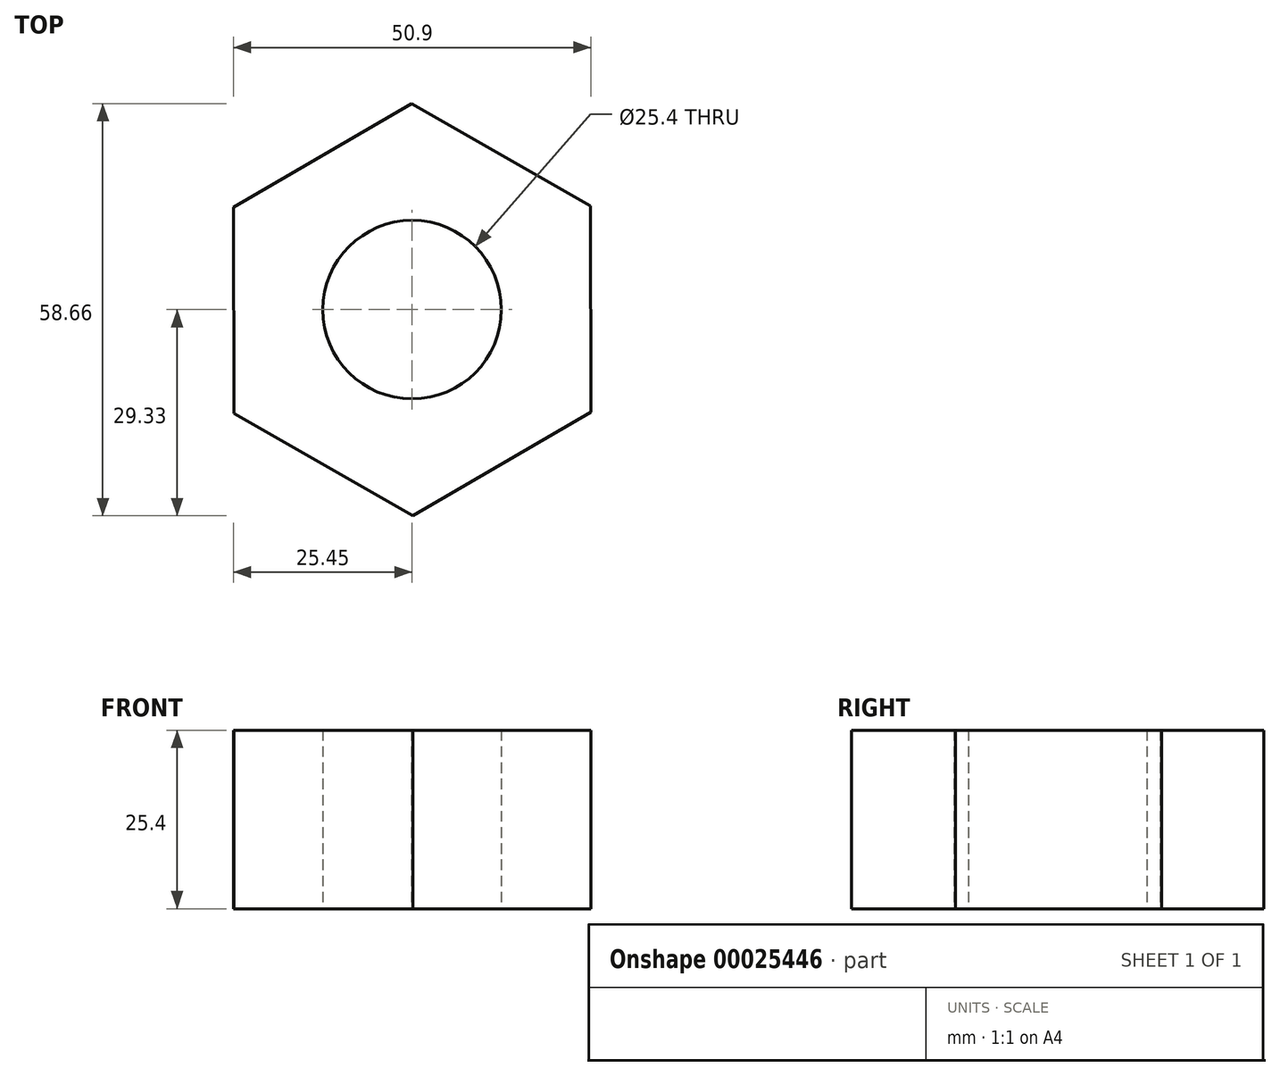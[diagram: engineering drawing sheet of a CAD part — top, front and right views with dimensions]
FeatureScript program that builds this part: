
annotation { "Feature Type Name" : "Feature", "Feature Type Description" : "" }
export const myFeature = defineFeature(function(context is Context, id is Id, definition is map)
    precondition{}
    {
        {
            var Q0;
            Q0=qCreatedBy(makeId("Top.planeOp"),FACE);
            var sketch = newSketch(context, id + "F0", { "sketchPlane" : qUnion([Q0])});
            skCircle(sketch, "E0", {"center": v(0, 0) * mm, "radius": 12.7 * mm});
            skCircle(sketch, "E1", {"center": v(0, 0) * mm, "radius": 25.4 * mm});
            skCircle(sketch, "E2.cCircle", {"center": v(0, 0) * mm, "radius": 25.4 * mm, "construction": true});
            skLineSegment(sketch, "E2.0", {"start": v(-25.45, 14.58) * mm, "end": v(-0.1, 29.33) * mm});
            skLineSegment(sketch, "E2.1", {"start": v(-0.1, 29.33) * mm, "end": v(25.35, 14.75) * mm});
            skLineSegment(sketch, "E2.2", {"start": v(25.35, 14.75) * mm, "end": v(25.45, -14.58) * mm});
            skLineSegment(sketch, "E2.3", {"start": v(25.45, -14.58) * mm, "end": v(0.1, -29.33) * mm});
            skLineSegment(sketch, "E2.4", {"start": v(0.1, -29.33) * mm, "end": v(-25.35, -14.75) * mm});
            skLineSegment(sketch, "E2.5", {"start": v(-25.35, -14.75) * mm, "end": v(-25.45, 14.58) * mm});
            skPoint(sketch, "E2.0.midPoint", {"position": v(-12.78, 21.95) * mm});
            skSolve(sketch);
        }
        {
            var Q0;
            Q0=makeQuery(id+"F0.imprint","IMPRINT",FACE,{"disambiguationData":[TD([[makeQuery(id+"F0.imprint","IMPRINT",EDGE,{"derivedFrom":sQuery(id+"F0.wireOp",EDGE,"E0")}),-1.0]])]});
            var Q1;
            {var subQ0=sQuery(id+"F0.wireOp",EDGE,"E2.5");var subQ1=sQuery(id+"F0.wireOp",EDGE,"E1");var subQ2=makeQuery(id+"F0.imprint","INTERSECT",VERTEX,{"derivedFrom":[subQ1,subQ0]});Q1=makeQuery(id+"F0.imprint","IMPRINT",FACE,{"disambiguationData":[TD([[makeQuery(id+"F0.imprint","IMPRINT",EDGE,{"disambiguationData":[TD([[subQ2,-1.0]])],"derivedFrom":subQ1}),-1.0]])]});}
            var Q2;
            {var subQ0=sQuery(id+"F0.wireOp",EDGE,"E2.4");var subQ1=sQuery(id+"F0.wireOp",EDGE,"E1");var subQ2=makeQuery(id+"F0.imprint","INTERSECT",VERTEX,{"derivedFrom":[subQ1,subQ0]});Q2=makeQuery(id+"F0.imprint","IMPRINT",FACE,{"disambiguationData":[TD([[makeQuery(id+"F0.imprint","IMPRINT",EDGE,{"disambiguationData":[TD([[subQ2,-1.0]])],"derivedFrom":subQ1}),-1.0]])]});}
            var Q3;
            {var subQ1=sQuery(id+"F0.wireOp",EDGE,"E1");var subQ3=sQuery(id+"F0.wireOp",EDGE,"E2.2");var subQ5=makeQuery(id+"F0.imprint","INTERSECT",VERTEX,{"derivedFrom":[subQ1,subQ3]});Q3=makeQuery(id+"F0.imprint","IMPRINT",FACE,{"disambiguationData":[TD([[makeQuery(id+"F0.imprint","IMPRINT",EDGE,{"disambiguationData":[TD([[subQ5,1.0]])],"derivedFrom":subQ1}),-1.0]])]});}
            var Q4;
            {var subQ1=sQuery(id+"F0.wireOp",EDGE,"E1");var subQ3=sQuery(id+"F0.wireOp",EDGE,"E2.0");var subQ5=makeQuery(id+"F0.imprint","INTERSECT",VERTEX,{"derivedFrom":[subQ1,subQ3]});Q4=makeQuery(id+"F0.imprint","IMPRINT",FACE,{"disambiguationData":[TD([[makeQuery(id+"F0.imprint","IMPRINT",EDGE,{"disambiguationData":[TD([[subQ5,-1.0]])],"derivedFrom":subQ1}),-1.0]])]});}
            var Q5;
            {var subQ0=sQuery(id+"F0.wireOp",EDGE,"E2.1");var subQ1=sQuery(id+"F0.wireOp",EDGE,"E1");var subQ2=makeQuery(id+"F0.imprint","INTERSECT",VERTEX,{"derivedFrom":[subQ1,subQ0]});Q5=makeQuery(id+"F0.imprint","IMPRINT",FACE,{"disambiguationData":[TD([[makeQuery(id+"F0.imprint","IMPRINT",EDGE,{"disambiguationData":[TD([[subQ2,-1.0]])],"derivedFrom":subQ1}),-1.0]])]});}
            var Q6;
            {var subQ1=sQuery(id+"F0.wireOp",EDGE,"E1");var subQ3=sQuery(id+"F0.wireOp",EDGE,"E2.1");var subQ5=makeQuery(id+"F0.imprint","INTERSECT",VERTEX,{"derivedFrom":[subQ1,subQ3]});Q6=makeQuery(id+"F0.imprint","IMPRINT",FACE,{"disambiguationData":[TD([[makeQuery(id+"F0.imprint","IMPRINT",EDGE,{"disambiguationData":[TD([[subQ5,1.0]])],"derivedFrom":subQ1}),-1.0]])]});}
            extrude(context, id + "F1", {"entities" : qUnion([Q0, Q1, Q2, Q3, Q4, Q5, Q6]), "depth" : 25.4 * mm});
        }
    });
